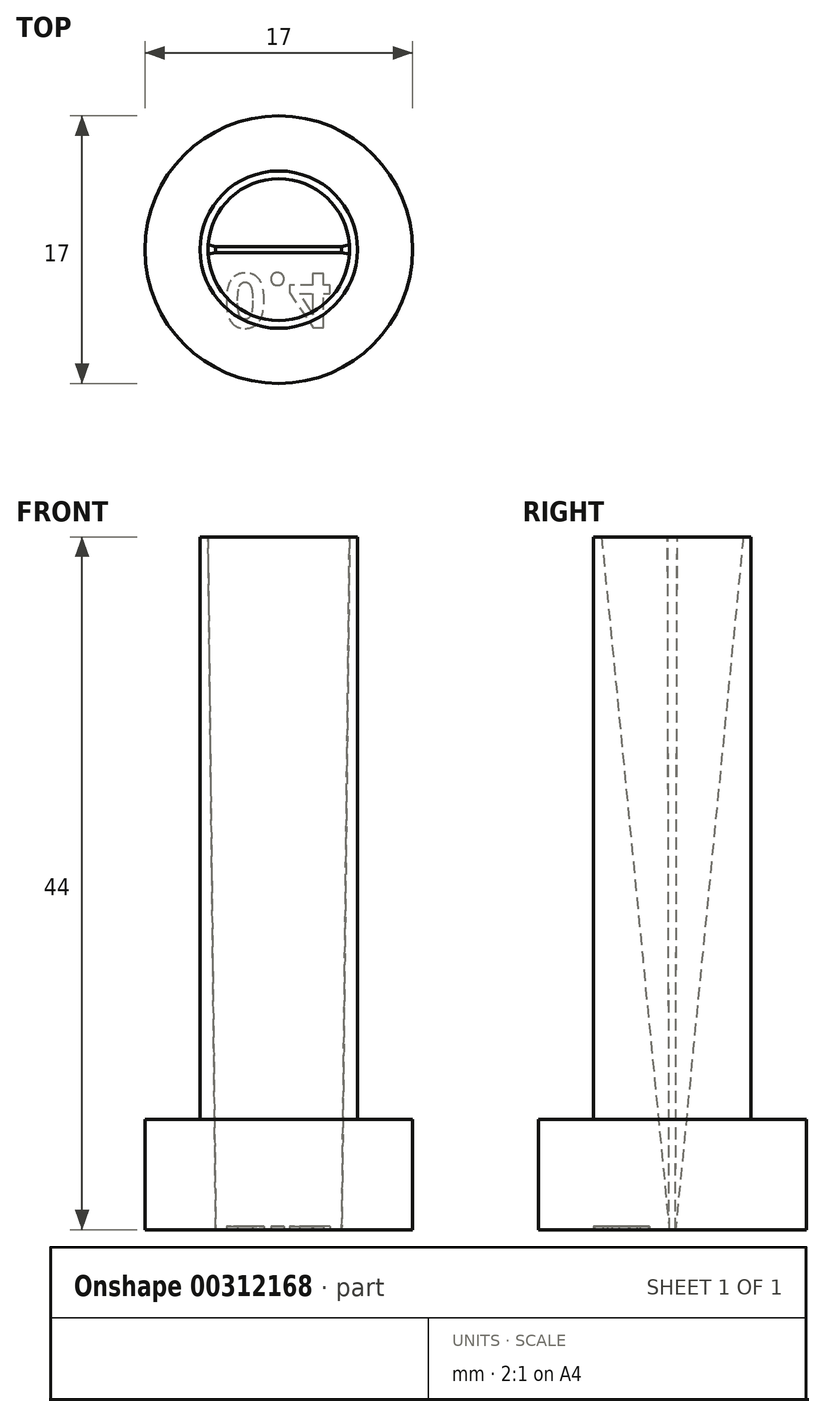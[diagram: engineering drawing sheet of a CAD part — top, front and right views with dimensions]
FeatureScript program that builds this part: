
annotation { "Feature Type Name" : "Feature", "Feature Type Description" : "" }
export const myFeature = defineFeature(function(context is Context, id is Id, definition is map)
    precondition{}
    {
        {
            var Q0;
            Q0=qCreatedBy(makeId("Top.planeOp"),FACE);
            var sketch = newSketch(context, id + "F0", { "sketchPlane" : qUnion([Q0])});
            skCircle(sketch, "E0", {"center": v(0, 0) * mm, "radius": 8.5 * mm});
            skSolve(sketch);
        }
        {
            var Q0;
            Q0=makeQuery(id+"F0.imprint","IMPRINT",FACE,{"disambiguationData":[TD([[makeQuery(id+"F0.imprint","IMPRINT",EDGE,{"derivedFrom":sQuery(id+"F0.wireOp",EDGE,"E0")}),1.0]])]});
            extrude(context, id + "F1", {"entities" : qUnion([Q0]), "depth" : 7 * mm});
        }
        {
            var Q0;
            Q0=makeQuery(id+"F1.opExtrude","CAP_FACE",FACE,{"disambiguationData":[OSD([sQuery(id+"F0.wireOp",EDGE,"E0")])],"isStart":false});
            var sketch = newSketch(context, id + "F2", { "sketchPlane" : qUnion([Q0])});
            skCircle(sketch, "E1", {"center": v(0, 0) * mm, "radius": 5 * mm});
            skSolve(sketch);
        }
        {
            var Q0;
            Q0=makeQuery(id+"F1.opExtrude","CAP_FACE",FACE,{"disambiguationData":[OSD([sQuery(id+"F0.wireOp",EDGE,"E0")])],"isStart":true});
            var sketch = newSketch(context, id + "F3", { "sketchPlane" : qUnion([Q0])});
            skPoint(sketch, "E2.middle", {"position": v(0, 0) * mm});
            skLineSegment(sketch, "E3.bottom", {"start": v(-4, 0.2) * mm, "end": v(4, 0.2) * mm});
            skLineSegment(sketch, "E3.top", {"start": v(-4, -0.2) * mm, "end": v(4, -0.2) * mm});
            skLineSegment(sketch, "E3.left", {"start": v(-4, 0.2) * mm, "end": v(-4, -0.2) * mm});
            skLineSegment(sketch, "E3.right", {"start": v(4, 0.2) * mm, "end": v(4, -0.2) * mm});
            skSolve(sketch);
        }
        {
            var Q0;
            Q0=makeQuery(id+"F2.imprint","IMPRINT",FACE,{"disambiguationData":[TD([[makeQuery(id+"F2.imprint","IMPRINT",EDGE,{"derivedFrom":sQuery(id+"F2.wireOp",EDGE,"E1")}),-1.0]])]});
            cPlane(context, id + "F4", {"entities" : qUnion([Q0]), "cplaneType" : CPlaneType.OFFSET, "offset" : 37 * mm, "width" : 150 * mm, "height" : 150 * mm});
        }
        {
            var Q0;
            Q0=qCreatedBy(id+"F4.planeOp",FACE);
            var sketch = newSketch(context, id + "F5", { "sketchPlane" : qUnion([Q0])});
            skArc(sketch, "E4", {"start": v(-4.49, -0.3) * mm, "mid": v(0, -4.5) * mm, "end": v(4.5, -0.3) * mm});
            skArc(sketch, "E5", {"start": v(4.5, -0.3) * mm, "mid": v(4.5, 0.01) * mm, "end": v(4.49, 0.32) * mm});
            skArc(sketch, "E6", {"start": v(4.49, 0.32) * mm, "mid": v(0, 4.5) * mm, "end": v(-4.49, 0.3) * mm});
            skArc(sketch, "E7", {"start": v(-4.49, 0.3) * mm, "mid": v(-4.5, 0) * mm, "end": v(-4.49, -0.3) * mm});
            skSolve(sketch);
        }
        {
            var Q0;
            Q0=makeQuery(id+"F2.imprint","IMPRINT",FACE,{"disambiguationData":[TD([[makeQuery(id+"F2.imprint","IMPRINT",EDGE,{"derivedFrom":sQuery(id+"F2.wireOp",EDGE,"E1")}),1.0]])]});
            extrude(context, id + "F6", {"entities" : qUnion([Q0]), "operationType" : NewBodyOperationType.ADD, "depth" : 37 * mm});
        }
        {
            var Q1;
            Q1=makeQuery(id+"F3.imprint","IMPRINT",FACE,{"disambiguationData":[TD([[makeQuery(id+"F3.imprint","IMPRINT",EDGE,{"derivedFrom":sQuery(id+"F3.wireOp",EDGE,"E3.bottom")}),-1.0]])]});
            var Q2;
            Q2=makeQuery(id+"F5.imprint","IMPRINT",FACE,{"disambiguationData":[TD([[makeQuery(id+"F5.imprint","IMPRINT",EDGE,{"derivedFrom":sQuery(id+"F5.wireOp",EDGE,"E4")}),1.0]])]});
            loft(context, id + "F7", {"operationType" : NewBodyOperationType.REMOVE, "sheetProfilesArray" : [{ "sheetProfileEntities" : qUnion([Q1]) }, { "sheetProfileEntities" : qUnion([Q2]) }]});
        }
        {
            var Q0;
            Q0=makeQuery(id+"F3.imprint","IMPRINT",FACE,{"disambiguationData":[TD([[makeQuery(id+"F3.imprint","IMPRINT",EDGE,{"derivedFrom":sQuery(id+"F3.wireOp",EDGE,"E3.bottom")}),1.0]])]});
            var sketch = newSketch(context, id + "F8", { "sketchPlane" : qUnion([Q0])});
            skText(sketch, "E8", { "text": "0.4", "fontName": "OpenSans-Bold.ttf"});
            const initialGuessF8  = {"E8": [-0.0035, 0.00153, 1, 0, 0.00345]};
            skSetInitialGuess(sketch, initialGuessF8);
            skSolve(sketch);
        }
        {
            var Q0;
            Q0 = qSketchRegion(id + "F8", true);
            extrude(context, id + "F9", {"entities" : qUnion([Q0]), "operationType" : NewBodyOperationType.REMOVE, "oppositeDirection" : true, "depth" : .2 * mm});
        }
    });
